# Revit family: RN 88021 Optipress-Gaz-Réduction
name_source: partatom
category: Rohrformteile
units: mm (PartAtom-declared; Revit-internal decimal feet)

## family parameters
Arbeitsebenenbasiert = Nein
Beim Laden mit Abzugskörper schneiden = Nein
Bemaßung runder Anschluss = Durchmesser verwenden
Gemeinsam genutzt = Ja
Immer vertikal = Ja
OmniClass-Nummer = 23.60.30.11.14
OmniClass-Titel = Pipework Fittings
Teiletyp = Übergang

## types (2) — shared parameters
Beschreibung = Reduzierstück
Hersteller = R. Nussbaum AG
IfcDescription = Reduzierstück
IfcExportAs = IfcPipeFitting
IfcExportType = TRANSITION
RN_LOD = LOD 400
RN_Manufactur = R. Nussbaum AG
RN_Mat = Edelstahl 1.4401
RN_Serie = Optipress gaz
RN_tab = RN_88021
Typenkommentare = Optipress-Gaz-Réduction
URL = https://www.nussbaum.ch

## per-type parameters (varying)
| type | Bauelement | Modell | RN_Muffe |
| mit Muffe | 03.01.07.03 | 88021.31 | Ja |
| ohne Muffe |  | 88021.24 | Nein |

## geometry (parser evidence)
native form markers: Sweep x2
no freeform markers — native parametric forms only
